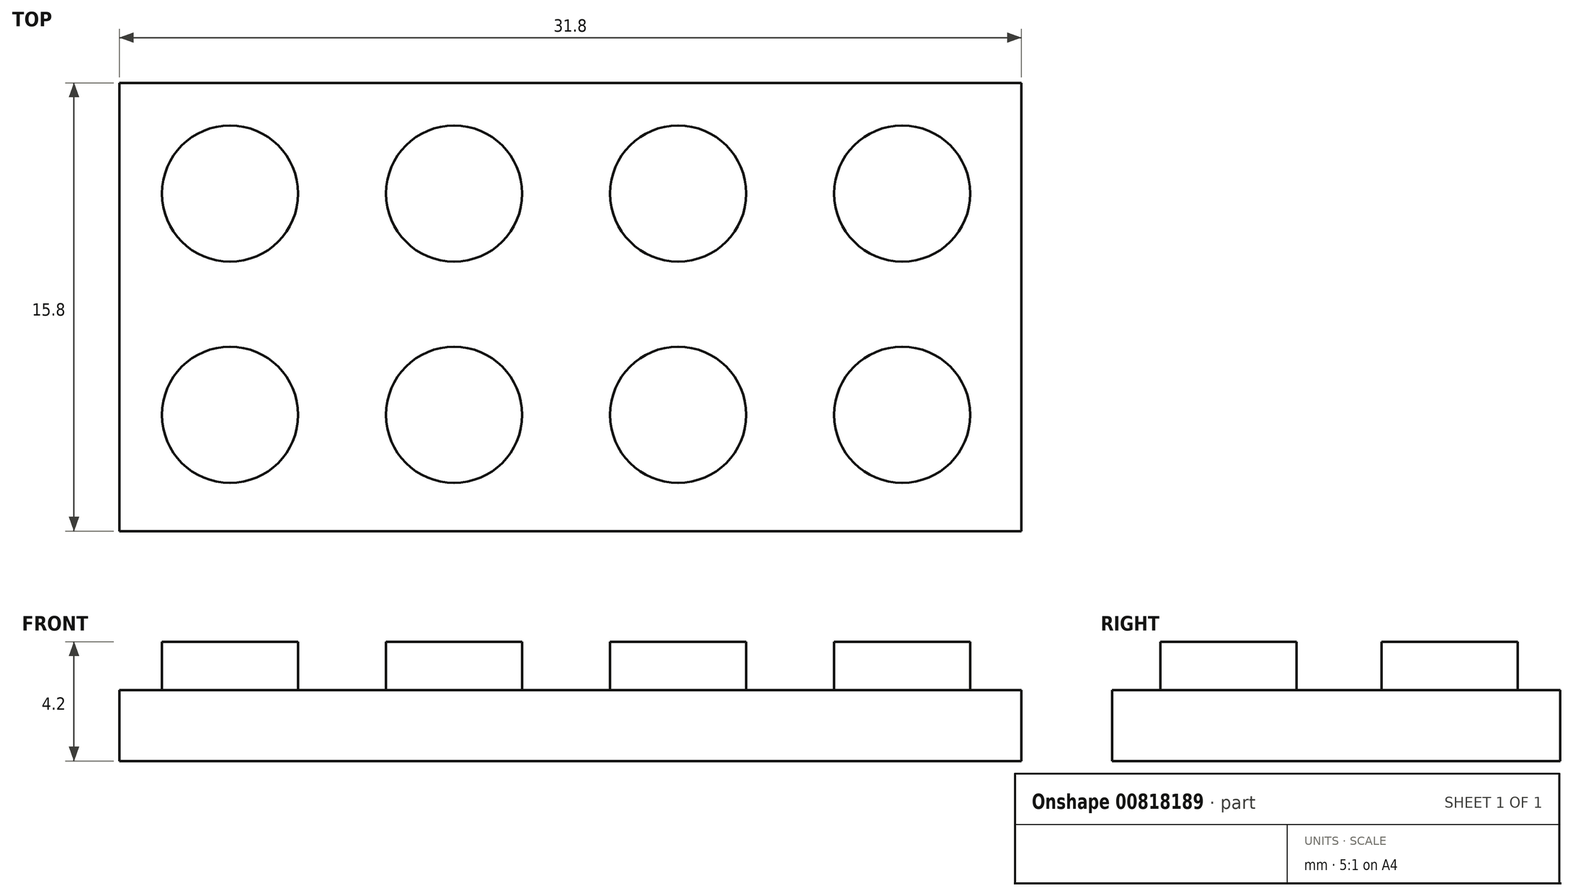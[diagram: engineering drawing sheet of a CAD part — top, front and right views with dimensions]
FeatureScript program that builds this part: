
annotation { "Feature Type Name" : "Feature", "Feature Type Description" : "" }
export const myFeature = defineFeature(function(context is Context, id is Id, definition is map)
    precondition{}
    {
        {
            var Q0;
            Q0=qCreatedBy(makeId("Top.planeOp"),FACE);
            var sketch = newSketch(context, id + "F0", { "sketchPlane" : qUnion([Q0])});
            skLineSegment(sketch, "E0.bottom", {"start": v(-15.9, 7.9) * mm, "end": v(15.9, 7.9) * mm});
            skLineSegment(sketch, "E0.top", {"start": v(-15.9, -7.9) * mm, "end": v(15.9, -7.9) * mm});
            skLineSegment(sketch, "E0.left", {"start": v(-15.9, 7.9) * mm, "end": v(-15.9, -7.9) * mm});
            skLineSegment(sketch, "E0.right", {"start": v(15.9, 7.9) * mm, "end": v(15.9, -7.9) * mm});
            skPoint(sketch, "E0.middle", {"position": v(0, 0) * mm});
            skSolve(sketch);
        }
        {
            var Q0;
            Q0=makeQuery(id+"F0.imprint","IMPRINT",FACE,{"disambiguationData":[TD([[makeQuery(id+"F0.imprint","IMPRINT",EDGE,{"derivedFrom":sQuery(id+"F0.wireOp",EDGE,"E0.bottom")}),-1.0]])]});
            extrude(context, id + "F1", {"entities" : qUnion([Q0]), "depth" : 2.5 * mm, "offsetDistance" : 25 * mm});
        }
        {
            var Q0;
            Q0=makeQuery(id+"F1.opExtrude","CAP_FACE",FACE,{"disambiguationData":[OSD([sQuery(id+"F0.wireOp",EDGE,"E0.bottom"),sQuery(id+"F0.wireOp",EDGE,"E0.top"),sQuery(id+"F0.wireOp",EDGE,"E0.left"),sQuery(id+"F0.wireOp",EDGE,"E0.right")])],"isStart":false});
            var sketch = newSketch(context, id + "F2", { "sketchPlane" : qUnion([Q0])});
            skCircle(sketch, "E1", {"center": v(-12, 4) * mm, "radius": 2.4 * mm});
            skCircle(sketch, "E2.0.1.0", {"center": v(-12, -3.8) * mm, "radius": 2.4 * mm});
            skCircle(sketch, "E2.1.0.0", {"center": v(-4.1, 4) * mm, "radius": 2.4 * mm});
            skCircle(sketch, "E2.1.1.0", {"center": v(-4.1, -3.8) * mm, "radius": 2.4 * mm});
            skCircle(sketch, "E2.2.0.0", {"center": v(3.8, 4) * mm, "radius": 2.4 * mm});
            skCircle(sketch, "E2.2.1.0", {"center": v(3.8, -3.8) * mm, "radius": 2.4 * mm});
            skCircle(sketch, "E2.3.0.0", {"center": v(11.7, 4) * mm, "radius": 2.4 * mm});
            skCircle(sketch, "E2.3.1.0", {"center": v(11.7, -3.8) * mm, "radius": 2.4 * mm});
            skLineSegment(sketch, "E2.direction1", {"start": v(-12, 4) * mm, "end": v(-4.1, 4) * mm, "construction": true});
            skLineSegment(sketch, "E2.direction2", {"start": v(-12, 4) * mm, "end": v(-12, -3.8) * mm, "construction": true});
            skSolve(sketch);
        }
        {
            var Q0;
            Q0=makeQuery(id+"F2.imprint","IMPRINT",FACE,{"disambiguationData":[TD([[makeQuery(id+"F2.imprint","IMPRINT",EDGE,{"derivedFrom":sQuery(id+"F2.wireOp",EDGE,"E1")}),1.0]])]});
            var Q1;
            Q1=makeQuery(id+"F2.imprint","IMPRINT",FACE,{"disambiguationData":[TD([[makeQuery(id+"F2.imprint","IMPRINT",EDGE,{"derivedFrom":sQuery(id+"F2.wireOp",EDGE,"E2.0.1.0")}),1.0]])]});
            var Q2;
            Q2=makeQuery(id+"F2.imprint","IMPRINT",FACE,{"disambiguationData":[TD([[makeQuery(id+"F2.imprint","IMPRINT",EDGE,{"derivedFrom":sQuery(id+"F2.wireOp",EDGE,"E2.1.1.0")}),1.0]])]});
            var Q3;
            Q3=makeQuery(id+"F2.imprint","IMPRINT",FACE,{"disambiguationData":[TD([[makeQuery(id+"F2.imprint","IMPRINT",EDGE,{"derivedFrom":sQuery(id+"F2.wireOp",EDGE,"E2.1.0.0")}),1.0]])]});
            var Q4;
            Q4=makeQuery(id+"F2.imprint","IMPRINT",FACE,{"disambiguationData":[TD([[makeQuery(id+"F2.imprint","IMPRINT",EDGE,{"derivedFrom":sQuery(id+"F2.wireOp",EDGE,"E2.2.0.0")}),1.0]])]});
            var Q5;
            Q5=makeQuery(id+"F2.imprint","IMPRINT",FACE,{"disambiguationData":[TD([[makeQuery(id+"F2.imprint","IMPRINT",EDGE,{"derivedFrom":sQuery(id+"F2.wireOp",EDGE,"E2.3.1.0")}),1.0]])]});
            var Q6;
            Q6=makeQuery(id+"F2.imprint","IMPRINT",FACE,{"disambiguationData":[TD([[makeQuery(id+"F2.imprint","IMPRINT",EDGE,{"derivedFrom":sQuery(id+"F2.wireOp",EDGE,"E2.3.0.0")}),1.0]])]});
            var Q7;
            Q7=makeQuery(id+"F2.imprint","IMPRINT",FACE,{"disambiguationData":[TD([[makeQuery(id+"F2.imprint","IMPRINT",EDGE,{"derivedFrom":sQuery(id+"F2.wireOp",EDGE,"E2.2.1.0")}),1.0]])]});
            extrude(context, id + "F3", {"entities" : qUnion([Q0, Q1, Q2, Q3, Q4, Q5, Q6, Q7]), "operationType" : NewBodyOperationType.ADD, "depth" : 1.7 * mm, "offsetDistance" : 25 * mm});
        }
    });
